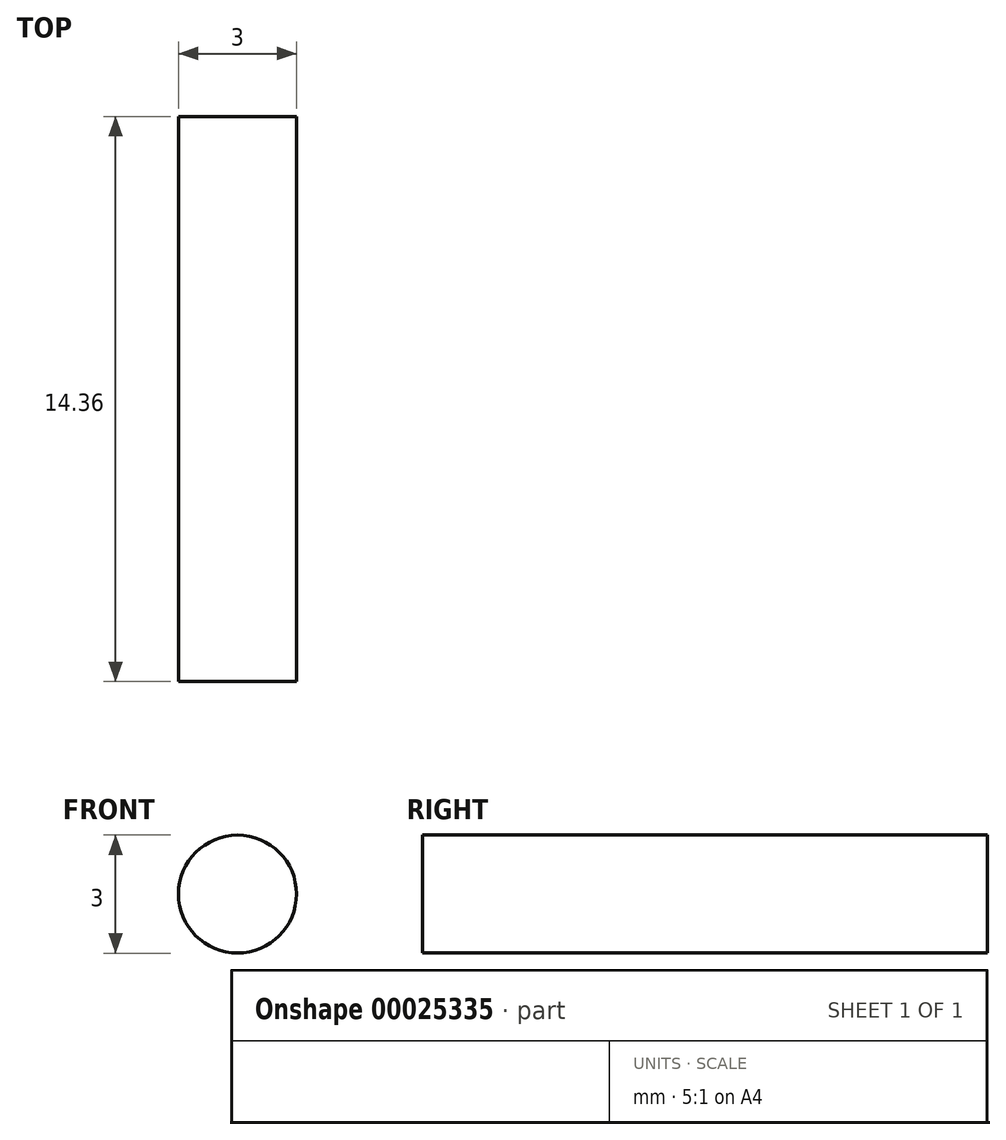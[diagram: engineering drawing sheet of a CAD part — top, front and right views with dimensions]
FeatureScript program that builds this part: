
annotation { "Feature Type Name" : "Feature", "Feature Type Description" : "" }
export const myFeature = defineFeature(function(context is Context, id is Id, definition is map)
    precondition{}
    {
        {
            var Q0;
            Q0=qCreatedBy(makeId("Front.planeOp"),FACE);
            var sketch = newSketch(context, id + "F0", { "sketchPlane" : qUnion([Q0])});
            skCircle(sketch, "E0", {"center": v(0, 0) * mm, "radius": 1.5 * mm});
            skSolve(sketch);
        }
        {
            var Q0;
            Q0 = qSketchRegion(id + "F0", true);
            extrude(context, id + "F1", {"entities" : qUnion([Q0]), "endBound" : BoundingType.SYMMETRIC, "depth" : 14.35 * mm});
        }
    });
